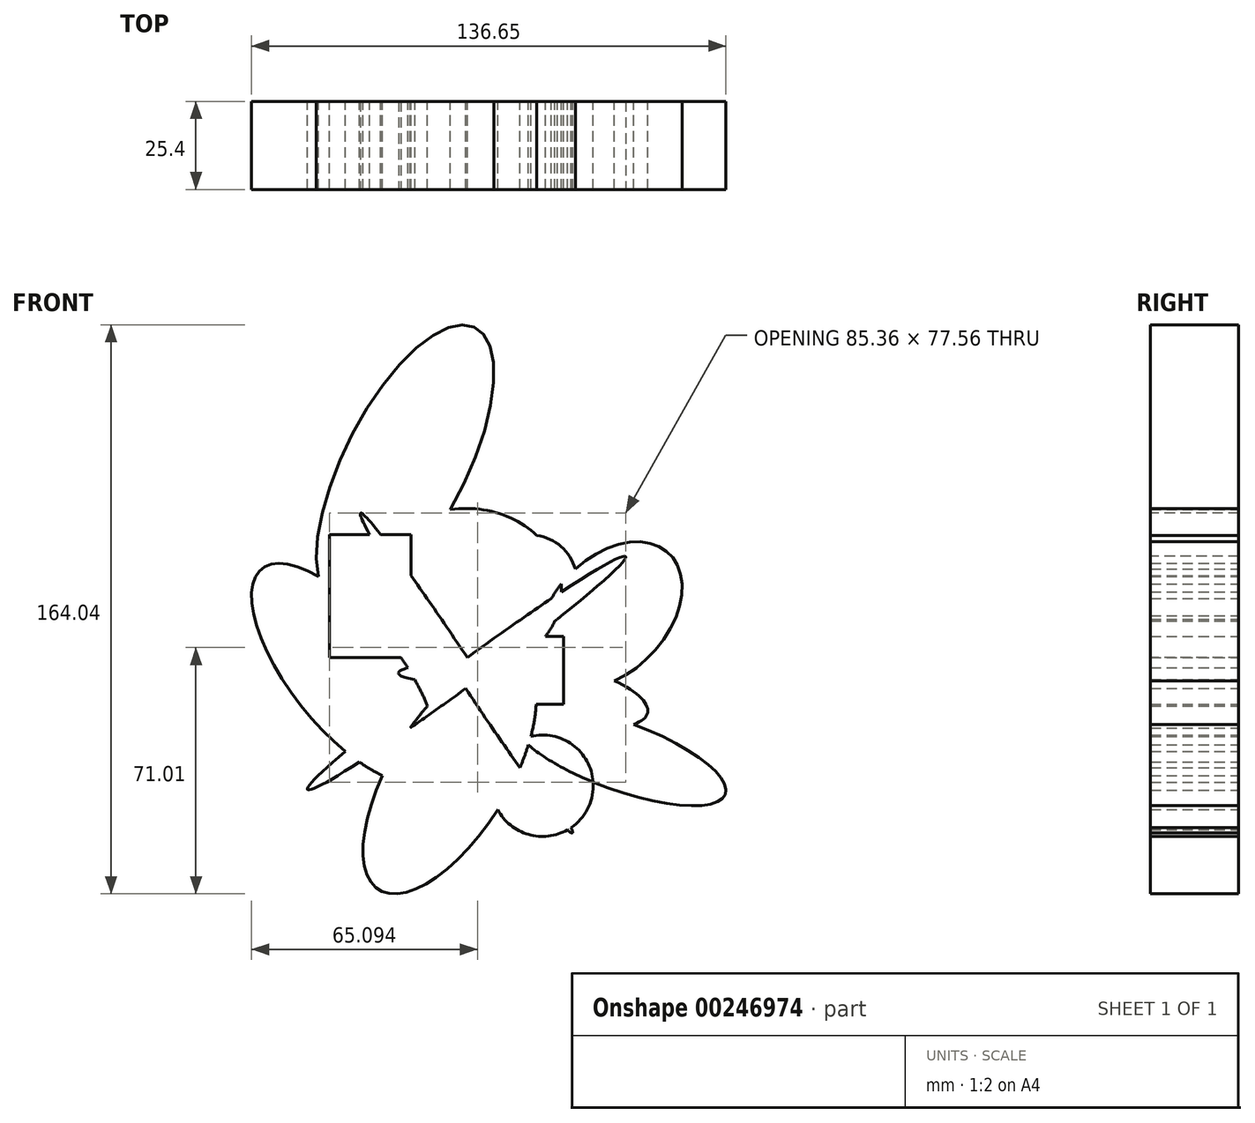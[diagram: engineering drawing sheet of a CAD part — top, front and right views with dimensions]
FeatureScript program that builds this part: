
annotation { "Feature Type Name" : "Feature", "Feature Type Description" : "" }
export const myFeature = defineFeature(function(context is Context, id is Id, definition is map)
    precondition{}
    {
        {
            var Q0;
            Q0=qCreatedBy(makeId("Front.planeOp"),FACE);
            var sketch = newSketch(context, id + "F0", { "sketchPlane" : qUnion([Q0])});
            skEllipse(sketch, "E0", {"center": v(0, 0) * mm, "majorRadius": 56.81 * mm, "minorRadius": 3.47 * mm, "majorAxis": v(0.8, 0.6)});
            skEllipse(sketch, "E1", {"center": v(0, 0) * mm, "majorRadius": 55.29 * mm, "minorRadius": 2.66 * mm, "majorAxis": v(0.55, -0.83)});
            skEllipse(sketch, "E2", {"center": v(0, 0) * mm, "majorRadius": 19.6 * mm, "minorRadius": 2.98 * mm, "majorAxis": v(1, 0)});
            skEllipse(sketch, "E3", {"center": v(0, 23.72) * mm, "majorRadius": 23.72 * mm, "minorRadius": 27.36 * mm, "majorAxis": v(0, -1)});
            skEllipse(sketch, "E4", {"center": v(26.08, -5.75) * mm, "majorRadius": 26.7 * mm, "minorRadius": 8.56 * mm, "majorAxis": v(-0.98, 0.22)});
            skEllipse(sketch, "E5", {"center": v(-4.86, -29.47) * mm, "majorRadius": 38.76 * mm, "minorRadius": 17 * mm, "majorAxis": v(0.52, 0.85)});
            skEllipse(sketch, "E6", {"center": v(-35.07, 0) * mm, "majorRadius": 38.38 * mm, "minorRadius": 15.7 * mm, "majorAxis": v(0.62, -0.78)});
            skCircle(sketch, "E7", {"center": v(18.5, 26.44) * mm, "radius": 13.33 * mm});
            skPoint(sketch, "E7.first.point", {"position": v(27.36, 36.4) * mm});
            skPoint(sketch, "E7.first.point.positionSnap0", {"position": v(27.36, 23.72) * mm});
            skPoint(sketch, "E7.second.point", {"position": v(27.36, 16.5) * mm});
            skPoint(sketch, "E7.second.point.positionSnap0", {"position": v(27.36, 23.72) * mm});
            skPoint(sketch, "E7.third.point", {"position": v(13.63, 14.03) * mm});
            skCircle(sketch, "E8", {"center": v(21.9, -32.47) * mm, "radius": 14.62 * mm});
            skPoint(sketch, "E8.first.point", {"position": v(15.62, -45.67) * mm});
            skPoint(sketch, "E8.second.point", {"position": v(31.23, -21.22) * mm});
            skPoint(sketch, "E8.third.point", {"position": v(34.03, -24.3) * mm});
            skPoint(sketch, "E9.firstSnap0", {"position": v(27.92, 2.61) * mm});
            skLineSegment(sketch, "E9.bottom", {"start": v(27.92, 10.6) * mm, "end": v(9.09, 10.6) * mm});
            skLineSegment(sketch, "E9.top", {"start": v(27.92, -9.05) * mm, "end": v(9.09, -9.05) * mm});
            skLineSegment(sketch, "E9.left", {"start": v(27.92, 10.6) * mm, "end": v(27.92, -9.05) * mm});
            skLineSegment(sketch, "E9.right", {"start": v(9.09, 10.6) * mm, "end": v(9.09, -9.05) * mm});
            skLineSegment(sketch, "E10.bottom", {"start": v(29.02, -19.3) * mm, "end": v(36.52, -19.3) * mm});
            skLineSegment(sketch, "E10.top", {"start": v(29.02, -32.47) * mm, "end": v(36.52, -32.47) * mm});
            skLineSegment(sketch, "E10.left", {"start": v(29.02, -19.3) * mm, "end": v(29.02, -32.47) * mm});
            skLineSegment(sketch, "E10.right", {"start": v(36.52, -19.3) * mm, "end": v(36.52, -32.47) * mm});
            skLineSegment(sketch, "E11.bottom", {"start": v(-39.5, 39.9) * mm, "end": v(-16.02, 39.9) * mm});
            skLineSegment(sketch, "E11.top", {"start": v(-39.5, 4.49) * mm, "end": v(-16.02, 4.49) * mm});
            skLineSegment(sketch, "E11.left", {"start": v(-39.5, 39.9) * mm, "end": v(-39.5, 4.49) * mm});
            skLineSegment(sketch, "E11.right", {"start": v(-16.02, 39.9) * mm, "end": v(-16.02, 4.49) * mm});
            skEllipse(sketch, "E12", {"center": v(41.4, 16.8) * mm, "majorRadius": 24.49 * mm, "minorRadius": 16.47 * mm, "majorAxis": v(-0.7, -0.72)});
            skEllipse(sketch, "E13", {"center": v(43.9, -23.72) * mm, "majorRadius": 32.63 * mm, "minorRadius": 9.86 * mm, "majorAxis": v(-0.94, 0.34)});
            skEllipse(sketch, "E14", {"center": v(-17.68, 59.96) * mm, "majorRadius": 44.48 * mm, "minorRadius": 17.6 * mm, "majorAxis": v(-0.45, -0.9)});
            skSolve(sketch);
        }
        {
            var Q0;
            Q0 = qSketchRegion(id + "F0", true);
            extrude(context, id + "F1", {"entities" : qUnion([Q0]), "depth" : 25.4 * mm});
        }
    });
